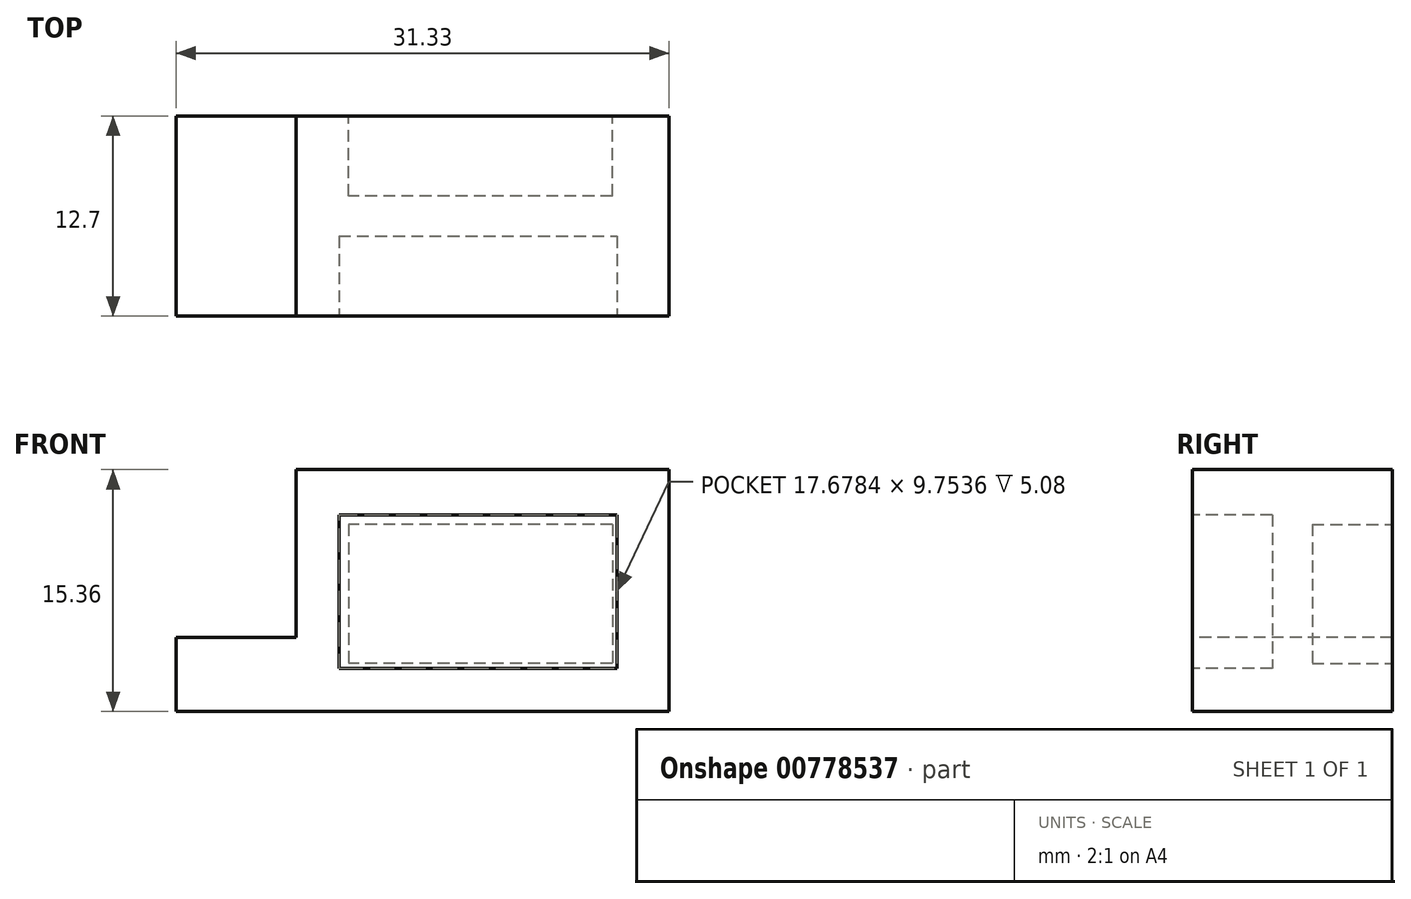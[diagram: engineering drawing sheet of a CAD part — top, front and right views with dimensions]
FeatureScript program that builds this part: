
annotation { "Feature Type Name" : "Feature", "Feature Type Description" : "" }
export const myFeature = defineFeature(function(context is Context, id is Id, definition is map)
    precondition{}
    {
        {
            var Q0;
            Q0=qCreatedBy(makeId("Front.planeOp"),FACE);
            var sketch = newSketch(context, id + "F0", { "sketchPlane" : qUnion([Q0])});
            skLineSegment(sketch, "E0.bottom", {"start": v(-11.72, 7.14) * mm, "end": v(11.99, 7.14) * mm});
            skLineSegment(sketch, "E0.top", {"start": v(-11.72, -8.22) * mm, "end": v(11.99, -8.22) * mm});
            skLineSegment(sketch, "E0.left", {"start": v(-11.72, 7.14) * mm, "end": v(-11.72, -8.22) * mm});
            skLineSegment(sketch, "E0.right", {"start": v(11.99, 7.14) * mm, "end": v(11.99, -8.22) * mm});
            skLineSegment(sketch, "E1.bottom", {"start": v(11.99, -8.22) * mm, "end": v(22.22, -8.22) * mm});
            skLineSegment(sketch, "E1.top", {"start": v(11.99, -2.56) * mm, "end": v(22.22, -2.56) * mm});
            skLineSegment(sketch, "E1.left", {"start": v(11.99, -8.22) * mm, "end": v(11.99, -2.56) * mm});
            skLineSegment(sketch, "E1.right", {"start": v(22.22, -8.22) * mm, "end": v(22.22, -2.56) * mm});
            skSolve(sketch);
        }
        {
            var Q0;
            Q0=makeQuery(id+"F0.imprint","IMPRINT",FACE,{"disambiguationData":[TD([[makeQuery(id+"F0.imprint","IMPRINT",EDGE,{"derivedFrom":sQuery(id+"F0.wireOp",EDGE,"E0.bottom")}),-1.0]])]});
            extrude(context, id + "F1", {"entities" : qUnion([Q0]), "depth" : 12.7 * mm, "offsetDistance" : 25.4 * mm});
        }
        {
            var Q0;
            Q0=makeQuery(id+"F1.opExtrude","CAP_FACE",FACE,{"disambiguationData":[OSD([sQuery(id+"F0.wireOp",EDGE,"E0.bottom"),sQuery(id+"F0.wireOp",EDGE,"E0.top"),sQuery(id+"F0.wireOp",EDGE,"E0.left"),sQuery(id+"F0.wireOp",EDGE,"E0.right"),sQuery(id+"F0.wireOp",EDGE,"E1.left")])],"isStart":true});
            var sketch = newSketch(context, id + "F2", { "sketchPlane" : qUnion([Q0])});
            skLineSegment(sketch, "E2.bottom", {"start": v(-9.92, 5.04) * mm, "end": v(9.5, 5.04) * mm});
            skLineSegment(sketch, "E2.top", {"start": v(-9.92, -6.29) * mm, "end": v(9.5, -6.29) * mm});
            skLineSegment(sketch, "E2.left", {"start": v(-9.92, 5.04) * mm, "end": v(-9.92, -6.29) * mm});
            skLineSegment(sketch, "E2.right", {"start": v(9.5, 5.04) * mm, "end": v(9.5, -6.29) * mm});
            skSolve(sketch);
        }
        {
            var Q0;
            Q0 = qSketchRegion(id + "F2", true);
            extrude(context, id + "F3", {"entities" : qUnion([Q0]), "operationType" : NewBodyOperationType.REMOVE, "oppositeDirection" : true, "depth" : 5.08 * mm, "offsetDistance" : 25.4 * mm});
        }
        {
            var Q0;
            Q0=makeQuery(id+"F1.opExtrude","SWEPT_FACE",FACE,{"disambiguationData":[OSD([sQuery(id+"F0.wireOp",EDGE,"E0.left")])]});
            var sketch = newSketch(context, id + "F4", { "sketchPlane" : qUnion([Q0])});
            skLineSegment(sketch, "E3.bottom", {"start": v(0, -8.22) * mm, "end": v(12.7, -8.22) * mm});
            skLineSegment(sketch, "E3.top", {"start": v(0, -3.52) * mm, "end": v(12.7, -3.52) * mm});
            skLineSegment(sketch, "E3.left", {"start": v(0, -8.22) * mm, "end": v(0, -3.52) * mm});
            skLineSegment(sketch, "E3.right", {"start": v(12.7, -8.22) * mm, "end": v(12.7, -3.52) * mm});
            skSolve(sketch);
        }
        {
            var Q0;
            Q0 = qSketchRegion(id + "F4", true);
            extrude(context, id + "F5", {"entities" : qUnion([Q0]), "operationType" : NewBodyOperationType.ADD, "depth" : 7.62 * mm, "offsetDistance" : 25.4 * mm});
        }
        {
            var Q0;
            Q0=makeQuery(id+"F3.boolean.opBoolean","COPY",FACE,{"derivedFrom":makeQuery(id+"F3.opExtrude","CAP_FACE",FACE,{"disambiguationData":[OSD([sQuery(id+"F2.wireOp",EDGE,"E2.bottom"),sQuery(id+"F2.wireOp",EDGE,"E2.top"),sQuery(id+"F2.wireOp",EDGE,"E2.left"),sQuery(id+"F2.wireOp",EDGE,"E2.right")])],"isStart":false})});
            extrude(context, id + "F6", {"entities" : qUnion([Q0]), "operationType" : NewBodyOperationType.ADD, "depth" : 5.08 * mm, "offsetDistance" : 25.4 * mm});
        }
        {
            var Q0;
            Q0=makeQuery(id+"F5.boolean.opBoolean","MERGE",FACE,{"derivedFrom":[makeQuery(id+"F1.opExtrude","CAP_FACE",FACE,{"disambiguationData":[OSD([sQuery(id+"F0.wireOp",EDGE,"E0.bottom"),sQuery(id+"F0.wireOp",EDGE,"E0.top"),sQuery(id+"F0.wireOp",EDGE,"E0.left"),sQuery(id+"F0.wireOp",EDGE,"E0.right"),sQuery(id+"F0.wireOp",EDGE,"E1.left")])],"isStart":false}),makeQuery(id+"F5.opExtrude","SWEPT_FACE",FACE,{"disambiguationData":[OSD([sQuery(id+"F4.wireOp",EDGE,"E3.right")])]})]});
            var sketch = newSketch(context, id + "F7", { "sketchPlane" : qUnion([Q0])});
            skLineSegment(sketch, "E4.bottom", {"start": v(-9, 4.27) * mm, "end": v(8.69, 4.27) * mm});
            skLineSegment(sketch, "E4.top", {"start": v(-9, -5.49) * mm, "end": v(8.69, -5.49) * mm});
            skLineSegment(sketch, "E4.left", {"start": v(-9, 4.27) * mm, "end": v(-9, -5.49) * mm});
            skLineSegment(sketch, "E4.right", {"start": v(8.69, 4.27) * mm, "end": v(8.69, -5.49) * mm});
            skSolve(sketch);
        }
        {
            var Q0;
            Q0 = qSketchRegion(id + "F7", true);
            extrude(context, id + "F8", {"entities" : qUnion([Q0]), "operationType" : NewBodyOperationType.REMOVE, "oppositeDirection" : true, "depth" : 5.08 * mm, "offsetDistance" : 25.4 * mm});
        }
        {
            var Q0;
            Q0=makeQuery(id+"F6.boolean.opBoolean","MERGE",FACE,{"derivedFrom":[makeQuery(id+"F5.boolean.opBoolean","MERGE",FACE,{"derivedFrom":[makeQuery(id+"F1.opExtrude","CAP_FACE",FACE,{"disambiguationData":[OSD([sQuery(id+"F0.wireOp",EDGE,"E0.bottom"),sQuery(id+"F0.wireOp",EDGE,"E0.top"),sQuery(id+"F0.wireOp",EDGE,"E0.left"),sQuery(id+"F0.wireOp",EDGE,"E0.right"),sQuery(id+"F0.wireOp",EDGE,"E1.left")])],"isStart":true}),makeQuery(id+"F5.opExtrude","SWEPT_FACE",FACE,{"disambiguationData":[OSD([sQuery(id+"F4.wireOp",EDGE,"E3.left")])]})]}),makeQuery(id+"F6.opExtrude","CAP_FACE",FACE,{"disambiguationData":[OSD([sQuery(id+"F2.wireOp",EDGE,"E2.bottom"),sQuery(id+"F2.wireOp",EDGE,"E2.top"),sQuery(id+"F2.wireOp",EDGE,"E2.left"),sQuery(id+"F2.wireOp",EDGE,"E2.right")])],"isStart":false})]});
            var sketch = newSketch(context, id + "F9", { "sketchPlane" : qUnion([Q0])});
            skLineSegment(sketch, "E5.bottom", {"start": v(-8.38, 3.66) * mm, "end": v(8.38, 3.66) * mm});
            skLineSegment(sketch, "E5.top", {"start": v(-8.38, -5.18) * mm, "end": v(8.38, -5.18) * mm});
            skLineSegment(sketch, "E5.left", {"start": v(-8.38, 3.66) * mm, "end": v(-8.38, -5.18) * mm});
            skLineSegment(sketch, "E5.right", {"start": v(8.38, 3.66) * mm, "end": v(8.38, -5.18) * mm});
            skSolve(sketch);
        }
        {
            var Q0;
            Q0 = qSketchRegion(id + "F9", true);
            extrude(context, id + "F10", {"entities" : qUnion([Q0]), "operationType" : NewBodyOperationType.REMOVE, "oppositeDirection" : true, "depth" : 5.08 * mm, "offsetDistance" : 25.4 * mm});
        }
    });
